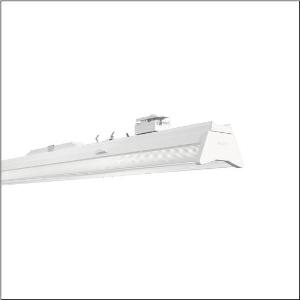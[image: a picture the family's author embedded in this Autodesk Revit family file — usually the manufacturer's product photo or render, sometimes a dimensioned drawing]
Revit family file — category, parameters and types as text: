
# Revit family: licross_11_performance_tw_51tm16tnt45x
name_source: partatom
category: Lighting Fixtures
units: mm (PartAtom-declared; Revit-internal decimal feet)

## family parameters
Cut with Voids When Loaded = No
Host = Face
Light Source = No
Part Type = Normal
Room Calculation Point = No
Round Connector Dimension = Use Diameter
Shared = No

## types (1)
- --- (1 x LED 2700 K ... 6500 K, 4700 lm, 28.9 W, 2700K)
    Apparent Load = 29 VA
    CIE Flux Codes = 63 87 95 78 100
    Color Rendering = 80
    Color Temperature = 2700K
    Default Elevation = 1800 mm
    Description = Licross 11 Performance TW, luminaire insert, of sheet steel, galvanised, coil coated, white, length: 1.500mm, width: 120mm, height: 123mm, LED rated luminous flux: 4.700lm, light colour: 8tw, SDCM (Standard Deviation of Colour Matching)MacAdam ≤ 2 SDCM (initial), control gear: DALI DT8, with plug, 5-pole, with phase selection, mains connection: 220..240V, AC, 50/60Hz, rated input power: 28.9W, internal wiring halogen-free, primary light control with lens, of plastic, primary optical cover: cover, of PMMA, light emission: direct/indirect distribution, primary light characteristic: symmetric, protection rating (complete): IP40, insulation class (complete): insulation class I (protective earthing), certification: CE, ENEC, VDE, UKCA, protection symbol: D if used in an environment without relevant dust loads with corresponding accessories, impact resistance: IK06, permissible ambient temperature for indoor applications: -25..+45°C, corresponds to IFS (International Featured Standards) requirements for safety and quality in the food industry, reducing of maximum allowable ambient temperature of 5°C with ceiling mounting, LABS conformity tested according to VDMA 24364:2018-05, The light source and the operating device comply with the requirements of the Ecodesign Regulation (EU) 2019/2020 and are replaceable in accordance with this regulation, packaging unit: 1 piece
    Height = 114 mm
    Lamp = 1 x LED 2700 K ... 6500 K
    Lamp Light Flux = 4700 lm
    Lamp Power = 28.9 W
    Lamp count = 1
    Length = 1500 mm
    Luminous efficacy = 163 lm/W
    Manufacturer = Siteco
    ModVariant = No
    Model = 51TM16TNT45X
    Mounting Place = Ceiling
    Mounting Type = Pendant
    Number of Poles = 1
    OnlyDefault = Yes
    Power Factor = 1
    Product Name = Licross 11 Performance TW
    Product group = luminaire insert | ceiling pendant
    ProductGroupID = 901
    Protection Class = Protection class I
    Protection Degree = IP 40
    RLX_Detail_Level = 1
    RLX_Emergency_Light_Flux = 0 lm
    RLX_Emergency_Type = 0
    RLX_Emergency_Type_DB = No
    RlxData = <blob elided: 30613 chars, md5=20010b3e>
    Socket = socket
    Standby Power = 0 W
    System Light Flux = 4700 lm
    System Power = 29 W
    Type Comments = individual setting: CCT=2700K
    Type Image = l_1256138.jpg
    URL = http://relux.com
    VarID = @adj_057921
    Voltage = 0 V
    Weight = 0.00 kg
    Width = 120 mm

## geometry (parser evidence)
native form markers: Blend x4, Sweep x13
no freeform markers — native parametric forms only
